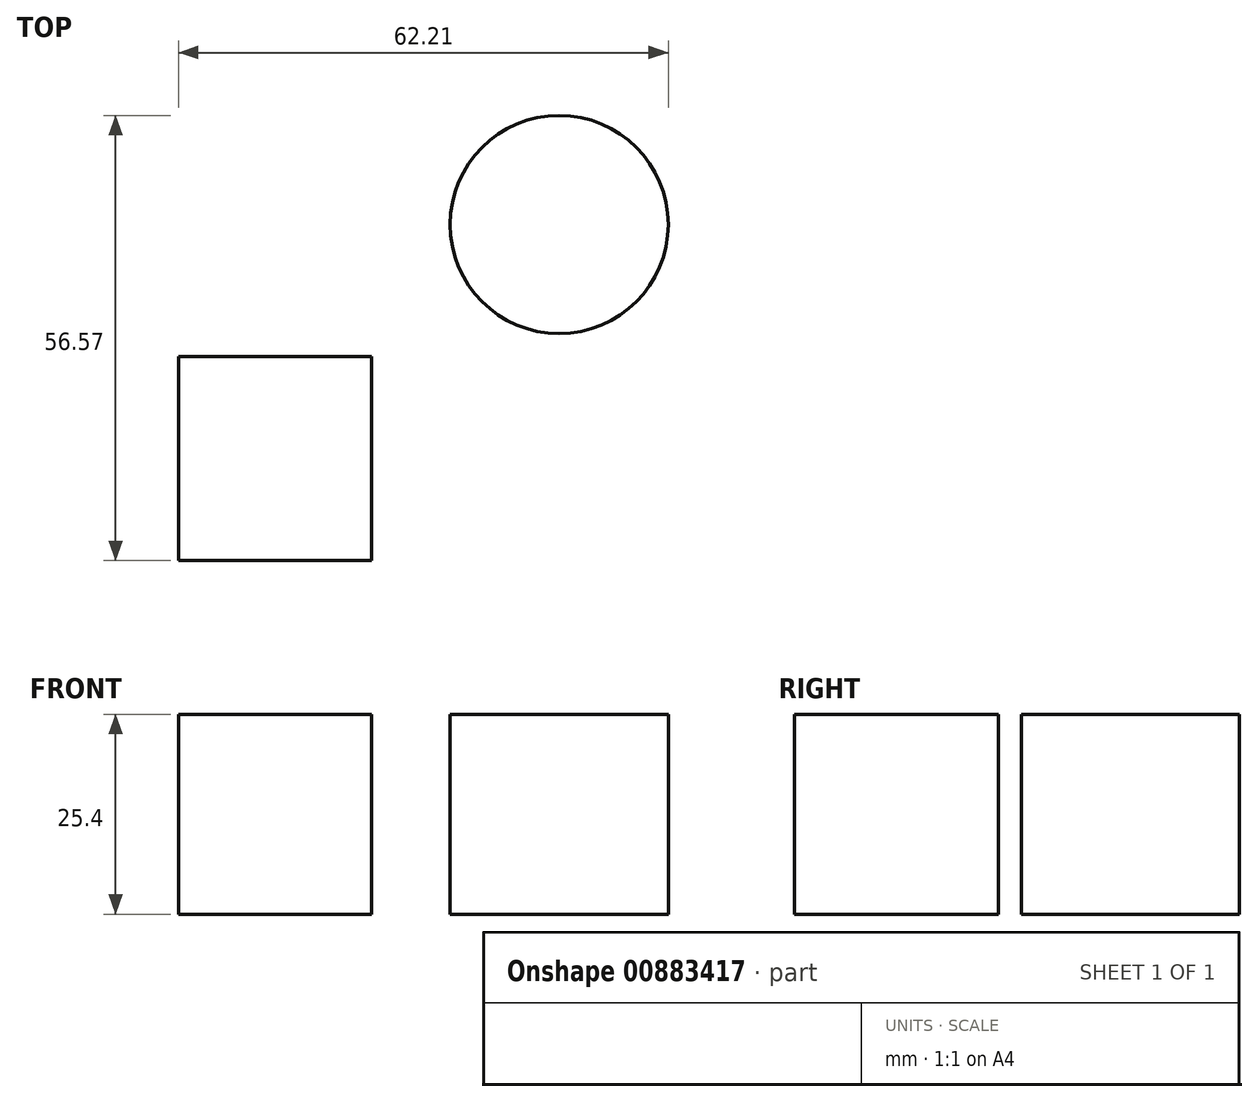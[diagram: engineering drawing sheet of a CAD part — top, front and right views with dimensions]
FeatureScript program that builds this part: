
annotation { "Feature Type Name" : "Feature", "Feature Type Description" : "" }
export const myFeature = defineFeature(function(context is Context, id is Id, definition is map)
    precondition{}
    {
        {
            var Q0;
            Q0=qCreatedBy(makeId("Top.planeOp"),FACE);
            var sketch = newSketch(context, id + "F0", { "sketchPlane" : qUnion([Q0])});
            skCircle(sketch, "E0", {"center": v(0, 0) * mm, "radius": 13.86 * mm});
            skSolve(sketch);
        }
        {
            var Q0;
            Q0 = qSketchRegion(id + "F0", true);
            extrude(context, id + "F1", {"entities" : qUnion([Q0]), "depth" : 25.4 * mm, "offsetDistance" : 25.4 * mm});
        }
        {
            var Q0;
            Q0=qCreatedBy(makeId("Top.planeOp"),FACE);
            var sketch = newSketch(context, id + "F2", { "sketchPlane" : qUnion([Q0])});
            skLineSegment(sketch, "E1.bottom", {"start": v(-48.35, -16.78) * mm, "end": v(-23.84, -16.78) * mm});
            skLineSegment(sketch, "E1.top", {"start": v(-48.35, -42.7) * mm, "end": v(-23.84, -42.7) * mm});
            skLineSegment(sketch, "E1.left", {"start": v(-48.35, -16.78) * mm, "end": v(-48.35, -42.7) * mm});
            skLineSegment(sketch, "E1.right", {"start": v(-23.84, -16.78) * mm, "end": v(-23.84, -42.7) * mm});
            skSolve(sketch);
        }
        {
            var Q0;
            Q0 = qSketchRegion(id + "F2", true);
            extrude(context, id + "F3", {"entities" : qUnion([Q0]), "depth" : 25.4 * mm, "offsetDistance" : 25.4 * mm});
        }
    });
